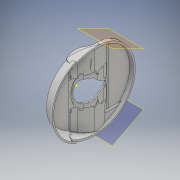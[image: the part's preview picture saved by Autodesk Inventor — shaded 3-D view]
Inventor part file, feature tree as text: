
AUTODESK INVENTOR PART (.ipt)
format: ipt  version: 2018 (Build 220112000, 112)  size: 2,409,472 bytes
history: native  units: mm
features: sketch x68, extrude x62, fillet x20, plane x2, revolve x1, mirror x1
ambient origin geometry x8: Origin, YZ Plane, XZ Plane, XY Plane, X Axis, Y Axis, Z Axis, Center Point
bodies: Solid1 (feature_tree)
feature tree (154):
  extrude  "Extrusion1"  TaperAngle=0.0deg  [1 undecoded]
  extrude  "Extrusion2"  Depth=10.0mm TaperAngle=0.0deg
  extrude  "Extrusion3"  Depth=10.0mm
  extrude  "Extrusion4"  TaperAngle=0.0deg  [1 undecoded]
  extrude  "Extrusion5"  Depth=10.0mm TaperAngle=0.0deg
  sketch  "Sketch6"  dims[d19=10.0mm d20=0.0mm d21=40.0mm]
  extrude  "Extrusion6"  Depth=10.0mm
  extrude  "Extrusion7"  Depth=11.0mm TaperAngle=0.0deg
  extrude  "Extrusion8"  Depth=32.0mm TaperAngle=0.0deg
  extrude  "Extrusion9"  Depth=32.0mm TaperAngle=0.0deg
  extrude  "Extrusion10"  Depth=10.0mm TaperAngle=0.0deg
  extrude  "Extrusion11"  Depth=10.0mm TaperAngle=0.0deg
  extrude  "Extrusion12"  TaperAngle=0.0deg  [1 undecoded]
  extrude  "Extrusion14"  Depth=48.3mm
  extrude  "Extrusion15"  TaperAngle=0.0deg  [1 undecoded]
  extrude  "Extrusion16"  Depth=10.0mm TaperAngle=0.0deg
  extrude  "Extrusion17"  Depth=11.63mm TaperAngle=0.0deg
  sketch  "Sketch21"  dims[d83=0.0mm d84=0.0mm d85=0.0mm d86=0.0mm]
  extrude  "Extrusion19"  Depth=11.63mm TaperAngle=0.0deg
  extrude  "Extrusion20"  TaperAngle=0.0deg  [1 undecoded]
  extrude  "Extrusion21"  Depth=10.0mm TaperAngle=0.0deg
  extrude  "Extrusion22"  TaperAngle=0.0deg  [1 undecoded]
  extrude  "Extrusion23"  Depth=2.86mm TaperAngle=0.0deg
  extrude  "Extrusion24"  Depth=2.01mm
  extrude  "Extrusion25"  Depth=10.0mm TaperAngle=0.0deg
  sketch  "Sketch33"  dims[d115=7.8mm d116=0.0mm d117=0.0mm d118=0.0mm]
  extrude  "Extrusion26"  Depth=10.0mm TaperAngle=0.0deg
  extrude  "Extrusion27"  TaperAngle=0.0deg  [1 undecoded]
  extrude  "Extrusion28"  Depth=22.0mm TaperAngle=0.0deg
  extrude  "Extrusion29"  Depth=17.0mm TaperAngle=0.0deg
  extrude  "Extrusion30"  Depth=2.0mm
  extrude  "Extrusion31"  Depth=2.0mm TaperAngle=0.0deg
  extrude  "Extrusion32"  Depth=18.0mm TaperAngle=0.0deg
  extrude  "Extrusion33"  Depth=1.02mm
  sketch  "Sketch42"  dims[d151=2.0mm d152=2.0mm]
  extrude  "Extrusion34"  Depth=7.72mm TaperAngle=0.0deg
  extrude  "Extrusion36"  Depth=2.0mm
  extrude  "Extrusion37"  Depth=2.0mm
  revolve  "Revolution3"  [1 undecoded]
  extrude  "Extrusion38"  Depth=2.0mm
  extrude  "Extrusion39"  Depth=10.0mm TaperAngle=0.0deg
  fillet  "Fillet1"  Radius=7.83mm
  fillet  "Fillet2"  Radius=20.0mm
  sketch  "Sketch51"  dims[d171=2.0mm d172=2.0mm]
  extrude  "Extrusion41"  Depth=6.4mm TaperAngle=0.0deg
  mirror  "Mirror1"
  extrude  "Extrusion42"  Depth=2.0mm
  sketch  "Sketch54"  dims[d179=18.4mm d180=0.0mm d181=2.0mm]
  sketch  "Sketch55"  dims[d182=2.0mm]
  sketch  "Sketch56"
  extrude  "Extrusion44"  Depth=2.0mm
  extrude  "Extrusion45"  Depth=2.0mm
  extrude  "Extrusion46"  Depth=18.4mm TaperAngle=0.0deg
  extrude  "Extrusion47"  Depth=2.0mm
  plane  "Work Plane2"
  extrude  "Extrusion48"  [1 undecoded]
  extrude  "Extrusion49"  [1 undecoded]
  plane  "Work Plane5"
  extrude  "Extrusion50"  [1 undecoded]
  extrude  "Extrusion51"  [1 undecoded]
  fillet  "Fillet3"  [1 undecoded]
  fillet  "Fillet4"  [1 undecoded]
  extrude  "Extrusion52"  [1 undecoded]
  extrude  "Extrusion53"  [1 undecoded]
  extrude  "Extrusion54"  [1 undecoded]
  extrude  "Extrusion55"  [1 undecoded]
  fillet  "Fillet5"  [1 undecoded]
  extrude  "Extrusion57"  [1 undecoded]
  extrude  "Extrusion58"  [1 undecoded]
  extrude  "Extrusion59"  [1 undecoded]
  fillet  "Fillet7"  [1 undecoded]
  fillet  "Fillet8"  [1 undecoded]
  fillet  "Fillet9"  [1 undecoded]
  fillet  "Fillet10"  [1 undecoded]
  fillet  "Fillet11"  [1 undecoded]
  fillet  "Fillet12"  [1 undecoded]
  fillet  "Fillet13"  [1 undecoded]
  fillet  "Fillet14"  [1 undecoded]
  extrude  "Extrusion60"  [1 undecoded]
  extrude  "Extrusion61"  [1 undecoded]
  extrude  "Extrusion62"  [1 undecoded]
  extrude  "Extrusion63"  [1 undecoded]
  extrude  "Extrusion64"  [1 undecoded]
  extrude  "Extrusion65"  [1 undecoded]
  fillet  "Fillet15"  [1 undecoded]
  fillet  "Fillet16"  [1 undecoded]
  fillet  "Fillet17"  [1 undecoded]
  fillet  "Fillet18"  [1 undecoded]
  fillet  "Fillet19"  [1 undecoded]
  extrude  "Extrusion66"  [1 undecoded]
  extrude  "Extrusion67"  [1 undecoded]
  extrude  "Extrusion68"  [1 undecoded]
  fillet  "Fillet20"  [1 undecoded]
  fillet  "Fillet21"  [1 undecoded]
  sketch  "Sketch1"  dims[d0=10.0mm d1=0.0mm d2=0.0mm d3=0.0mm]
  sketch  "Sketch2"  dims[d4=0.0mm d5=0.0mm d6=10.0mm d7=0.0mm]
  sketch  "Sketch3"  dims[d8=10.0mm d9=0.0mm d10=50.0mm]
  sketch  "Sketch4"  dims[d11=10.0mm d12=0.0mm d13=0.0mm d14=0.0mm]
  sketch  "Sketch5"  dims[d15=0.0mm d16=0.0mm d17=10.0mm d18=0.0mm]
  sketch  "Sketch7"  dims[d22=38.0mm d23=11.0mm d24=0.0mm]
  sketch  "Sketch8"  dims[d25=9.5mm d26=0.0mm d33=32.0mm d34=0.0mm]
  sketch  "Sketch9"  dims[d37=32.0mm d38=0.0mm d39=32.0mm d40=0.0mm]
  sketch  "Sketch10"  dims[d41=32.0mm d42=0.0mm d45=10.0mm d46=0.0mm]
  sketch  "Sketch11"  dims[d47=10.0mm d48=0.0mm d49=10.0mm d50=0.0mm]
  sketch  "Sketch12"  dims[d51=0.0mm d52=0.0mm d53=0.0mm d54=0.0mm]
  sketch  "Sketch13"  dims[d65=46.0mm d66=48.3mm]
  sketch  "Sketch16"  dims[d67=9.0mm d68=0.0mm d69=0.0mm d70=0.0mm]
  sketch  "Sketch18"  dims[d71=0.0mm d72=0.0mm d73=10.0mm d74=0.0mm]
  sketch  "Sketch19"  dims[d75=5.0mm d76=0.0mm d77=11.63mm d78=0.0mm]
  sketch  "Sketch20"  dims[d79=11.63mm d80=0.0mm d81=11.63mm d82=0.0mm]
  sketch  "Sketch22"  dims[d87=30.0mm d88=10.0mm d89=0.0mm]
  sketch  "Sketch23"  dims[d92=10.0mm d93=0.0mm d94=0.0mm d95=0.0mm]
  sketch  "Sketch24"  dims[d96=135.0deg d99=2.86mm d100=0.0mm]
  sketch  "Sketch25"  dims[d101=0.0mm d102=0.0mm d105=2.01mm]
  sketch  "Sketch31"  dims[d106=2.22mm d107=10.0mm d108=0.0mm]
  sketch  "Sketch32"  dims[d109=10.0mm d110=0.0mm d113=7.8mm d114=0.0mm]
  sketch  "Sketch34"  dims[d119=16.0mm d120=0.0mm d121=22.0mm d122=0.0mm]
  sketch  "Sketch35"  dims[d123=22.0mm d124=0.0mm d126=17.0mm d127=0.0mm]
  sketch  "Sketch36"  dims[d128=17.0mm d129=0.0mm d130=2.0mm]
  sketch  "Sketch37"  dims[d131=2.0mm d132=6.95mm d133=0.0mm]
  sketch  "Sketch38"  dims[d134=6.95mm d135=0.0mm d136=18.0mm d137=0.0mm]
  sketch  "Sketch39"  dims[d138=16.0mm d139=0.0mm d140=1.02mm]
  sketch  "Sketch40"  dims[d143=15.5mm d144=0.0mm d146=7.72mm d147=0.0mm]
  sketch  "Sketch41"  dims[d148=17.0mm d149=0.0mm d150=2.0mm]
  sketch  "Sketch43"  dims[d153=2.0mm d154=2.0mm]
  sketch  "Sketch45"  dims[d155=2.0mm d156=2.0mm]
  sketch  "Sketch47"  dims[d157=2.0mm d158=10.0mm d159=0.0mm d160=7.83mm d161=0.0mm d162=20.0mm d163=0.0mm]
  sketch  "Sketch48"  dims[d164=0.0mm d165=0.0mm d166=6.4mm d167=0.0mm]
  sketch  "Sketch49"  dims[d168=6.14mm d169=0.0mm d170=2.0mm]
  sketch  "Sketch52"  dims[d173=2.0mm d174=2.0mm]
  sketch  "Sketch53"  dims[d175=7.82mm d176=0.0mm d177=18.4mm d178=0.0mm]
  sketch  "Sketch57"
  sketch  "Sketch60"
  sketch  "Sketch61"
  sketch  "Sketch62"
  sketch  "Sketch63"
  sketch  "Sketch65"
  sketch  "Sketch66"
  sketch  "Sketch67"
  sketch  "Sketch68"
  sketch  "Sketch69"
  sketch  "Sketch70"
  sketch  "Sketch72"
  sketch  "Sketch73"
  sketch  "Sketch74"
  sketch  "Sketch75"
  sketch  "Sketch76"
  sketch  "Sketch78"
  sketch  "Sketch80"
  sketch  "Sketch81"
  sketch  "Sketch82"
  sketch  "Sketch83"
  sketch  "Sketch84"
  sketch  "Sketch85"
note: 46 required parameter values undecoded (feature->parameter linkage not recoverable at this tier; creation-order binding heuristic only, values carry confidence <= 0.55)